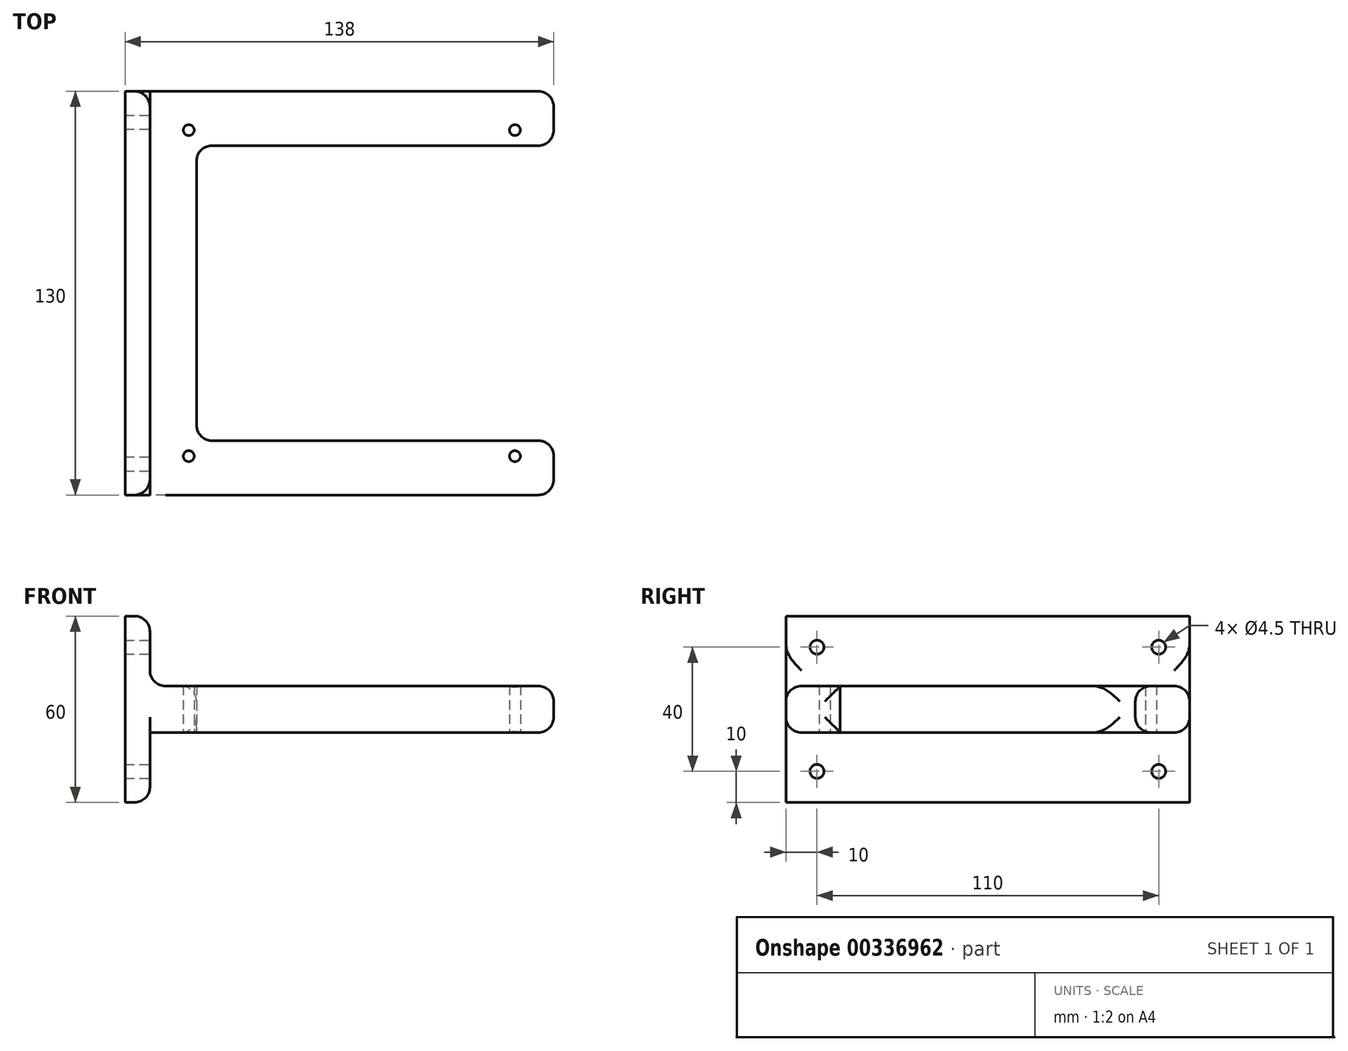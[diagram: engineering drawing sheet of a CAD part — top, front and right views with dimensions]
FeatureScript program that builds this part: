
annotation { "Feature Type Name" : "Feature", "Feature Type Description" : "" }
export const myFeature = defineFeature(function(context is Context, id is Id, definition is map)
    precondition{}
    {
        {
            var Q0;
            Q0=qCreatedBy(makeId("Top.planeOp"),FACE);
            var sketch = newSketch(context, id + "F0", { "sketchPlane" : qUnion([Q0])});
            skLineSegment(sketch, "E0.bottom", {"start": v(0, 0) * mm, "end": v(130, 0) * mm});
            skLineSegment(sketch, "E0.top", {"start": v(0, 130) * mm, "end": v(130, 130) * mm});
            skLineSegment(sketch, "E0.left", {"start": v(0, 0) * mm, "end": v(0, 130) * mm});
            skLineSegment(sketch, "E0.right", {"start": v(130, 0) * mm, "end": v(130, 130) * mm});
            skCircle(sketch, "E1", {"center": v(12.5, 12.5) * mm, "radius": 1.75 * mm});
            skCircle(sketch, "E2.0.1.0", {"center": v(12.5, 117.5) * mm, "radius": 1.75 * mm});
            skCircle(sketch, "E2.1.0.0", {"center": v(117.5, 12.5) * mm, "radius": 1.75 * mm});
            skCircle(sketch, "E2.1.1.0", {"center": v(117.5, 117.5) * mm, "radius": 1.75 * mm});
            skLineSegment(sketch, "E2.direction1", {"start": v(12.5, 12.5) * mm, "end": v(117.5, 12.5) * mm, "construction": true});
            skLineSegment(sketch, "E2.direction2", {"start": v(12.5, 12.5) * mm, "end": v(12.5, 117.5) * mm, "construction": true});
            skLineSegment(sketch, "E3.bottom", {"start": v(130, 112.5) * mm, "end": v(15, 112.5) * mm});
            skLineSegment(sketch, "E3.top", {"start": v(130, 17.5) * mm, "end": v(15, 17.5) * mm});
            skLineSegment(sketch, "E3.left", {"start": v(130, 112.5) * mm, "end": v(130, 17.5) * mm});
            skLineSegment(sketch, "E3.right", {"start": v(15, 112.5) * mm, "end": v(15, 17.5) * mm});
            skSolve(sketch);
        }
        {
            var Q0;
            {var subQ4=sQuery(id+"F0.wireOp",EDGE,"E0.bottom");Q0=makeQuery(id+"F0.imprint","IMPRINT",FACE,{"disambiguationData":[TD([[makeQuery(id+"F0.imprint","IMPRINT",EDGE,{"derivedFrom":subQ4}),1.0]])]});}
            extrude(context, id + "F1", {"entities" : qUnion([Q0]), "depth" : 15 * mm});
        }
        {
            var Q0;
            Q0=makeQuery(id+"F1.opExtrude","SWEPT_FACE",FACE,{"disambiguationData":[OSD([sQuery(id+"F0.wireOp",EDGE,"E0.left")])]});
            var sketch = newSketch(context, id + "F2", { "sketchPlane" : qUnion([Q0])});
            skPoint(sketch, "E4.oppositeSnap0", {"position": v(0, 7.5) * mm});
            skLineSegment(sketch, "E4.top", {"start": v(-130, 37.5) * mm, "end": v(0, 37.5) * mm});
            skLineSegment(sketch, "E4.left", {"start": v(-130, 7.5) * mm, "end": v(-130, 37.5) * mm});
            skLineSegment(sketch, "E4.right", {"start": v(0, 7.5) * mm, "end": v(0, 37.5) * mm});
            skLineSegment(sketch, "E5.top", {"start": v(0, -22.5) * mm, "end": v(-130, -22.5) * mm});
            skLineSegment(sketch, "E5.left", {"start": v(0, 7.5) * mm, "end": v(0, -22.5) * mm});
            skLineSegment(sketch, "E5.right", {"start": v(-130, 7.5) * mm, "end": v(-130, -22.5) * mm});
            skCircle(sketch, "E6", {"center": v(-120, -12.5) * mm, "radius": 2.25 * mm});
            skCircle(sketch, "E7.0.1.0", {"center": v(-120, 27.5) * mm, "radius": 2.25 * mm});
            skCircle(sketch, "E7.1.0.0", {"center": v(-10, -12.5) * mm, "radius": 2.25 * mm});
            skCircle(sketch, "E7.1.1.0", {"center": v(-10, 27.5) * mm, "radius": 2.25 * mm});
            skLineSegment(sketch, "E7.direction1", {"start": v(-120, -12.5) * mm, "end": v(-10, -12.5) * mm, "construction": true});
            skLineSegment(sketch, "E7.direction2", {"start": v(-120, -12.5) * mm, "end": v(-120, 27.5) * mm, "construction": true});
            skSolve(sketch);
        }
        {
            var Q0;
            {var subQ0=sQuery(id+"F2.wireOp",EDGE,"E5.top");Q0=makeQuery(id+"F2.imprint","IMPRINT",FACE,{"disambiguationData":[TD([[makeQuery(id+"F2.imprint","IMPRINT",EDGE,{"derivedFrom":subQ0}),-1.0]])]});}
            var Q1;
            {var subQ1=sQuery(id+"F0.wireOp",EDGE,"E0.left");var subQ2=makeQuery(id+"F1.opExtrude","CAP_EDGE",EDGE,{"disambiguationData":[OSD([subQ1])],"isStart":true});Q1=makeQuery(id+"F2.imprint","IMPRINT",FACE,{"disambiguationData":[TD([[makeQuery(id+"F2.imprint","IMPRINT",EDGE,{"derivedFrom":subQ2}),-1.0]])]});}
            var Q2;
            {var subQ0=sQuery(id+"F2.wireOp",EDGE,"E4.top");Q2=makeQuery(id+"F2.imprint","IMPRINT",FACE,{"disambiguationData":[TD([[makeQuery(id+"F2.imprint","IMPRINT",EDGE,{"derivedFrom":subQ0}),-1.0]])]});}
            extrude(context, id + "F3", {"entities" : qUnion([Q0, Q1, Q2]), "operationType" : NewBodyOperationType.ADD, "depth" : 8 * mm});
        }
        {
            var Q0;
            Q0=makeQuery(id+"F1.opExtrude","CAP_EDGE",EDGE,{"disambiguationData":[OSD([sQuery(id+"F0.wireOp",EDGE,"E0.left")])],"isStart":false});
            var Q1;
            Q1=makeQuery(id+"F1.opExtrude","CAP_EDGE",EDGE,{"disambiguationData":[OSD([sQuery(id+"F0.wireOp",EDGE,"E0.left")])],"isStart":true});
            var Q2;
            Q2=makeQuery(id+"F1.opExtrude","SWEPT_EDGE",EDGE,{"disambiguationData":[OSD([sQuery(id+"F0.wireOp",EDGE,"E3.bottom"),sQuery(id+"F0.wireOp",EDGE,"E3.right")])]});
            var Q3;
            Q3=makeQuery(id+"F1.opExtrude","SWEPT_EDGE",EDGE,{"disambiguationData":[OSD([sQuery(id+"F0.wireOp",EDGE,"E3.top"),sQuery(id+"F0.wireOp",EDGE,"E3.right")])]});
            var Q4;
            Q4=makeQuery(id+"F1.opExtrude","SWEPT_EDGE",EDGE,{"disambiguationData":[OSD([sQuery(id+"F0.wireOp",EDGE,"E0.right"),sQuery(id+"F0.wireOp",EDGE,"E3.top"),sQuery(id+"F0.wireOp",EDGE,"E3.left")])]});
            var Q5;
            Q5=makeQuery(id+"F1.opExtrude","SWEPT_EDGE",EDGE,{"disambiguationData":[OSD([sQuery(id+"F0.wireOp",EDGE,"E0.bottom"),sQuery(id+"F0.wireOp",EDGE,"E0.right")])]});
            var Q6;
            Q6=makeQuery(id+"F1.opExtrude","SWEPT_EDGE",EDGE,{"disambiguationData":[OSD([sQuery(id+"F0.wireOp",EDGE,"E0.top"),sQuery(id+"F0.wireOp",EDGE,"E0.right")])]});
            var Q7;
            Q7=makeQuery(id+"F1.opExtrude","SWEPT_EDGE",EDGE,{"disambiguationData":[OSD([sQuery(id+"F0.wireOp",EDGE,"E0.right"),sQuery(id+"F0.wireOp",EDGE,"E3.bottom"),sQuery(id+"F0.wireOp",EDGE,"E3.left")])]});
            var Q8;
            Q8=makeQuery(id+"F1.opExtrude","CAP_EDGE",EDGE,{"disambiguationData":[OSD([sQuery(id+"F0.wireOp",EDGE,"E3.bottom")])],"isStart":false});
            var Q9;
            Q9=makeQuery(id+"F1.opExtrude","CAP_EDGE",EDGE,{"disambiguationData":[OSD([sQuery(id+"F0.wireOp",EDGE,"E0.bottom")])],"isStart":false});
            var Q10;
            Q10=makeQuery(id+"F1.opExtrude","CAP_EDGE",EDGE,{"disambiguationData":[OSD([sQuery(id+"F0.wireOp",EDGE,"E0.top")])],"isStart":false});
            var Q11;
            Q11=makeQuery(id+"F3.opExtrude","CAP_EDGE",EDGE,{"disambiguationData":[OSD([sQuery(id+"F2.wireOp",EDGE,"E4.top")])],"isStart":true});
            var Q12;
            Q12=makeQuery(id+"F1.opExtrude","CAP_EDGE",EDGE,{"disambiguationData":[OSD([sQuery(id+"F0.wireOp",EDGE,"E0.bottom")])],"isStart":true});
            var Q13;
            Q13=makeQuery(id+"F3.opExtrude","CAP_EDGE",EDGE,{"disambiguationData":[OSD([sQuery(id+"F2.wireOp",EDGE,"E5.top")])],"isStart":true});
            var Q14;
            Q14=makeQuery(id+"F1.opExtrude","CAP_EDGE",EDGE,{"disambiguationData":[OSD([sQuery(id+"F0.wireOp",EDGE,"E0.top")])],"isStart":true});
            var Q15;
            {var subQ0=sQuery(id+"F0.wireOp",EDGE,"E0.right");Q15=makeQuery(id+"F1.opExtrude","CAP_EDGE",EDGE,{"disambiguationData":[OSD([subQ0]),TDD([makeQuery(id+"F0.imprint","IMPRINT",EDGE,{"disambiguationData":[TD([[makeQuery(id+"F0.imprint","INTERSECT",VERTEX,{"derivedFrom":[sQuery(id+"F0.wireOp",EDGE,"E0.bottom"),subQ0]}),-1.0]])],"derivedFrom":subQ0})])],"isStart":false});}
            var Q16;
            {var subQ0=sQuery(id+"F0.wireOp",EDGE,"E0.right");Q16=makeQuery(id+"F1.opExtrude","CAP_EDGE",EDGE,{"disambiguationData":[OSD([subQ0]),TDD([makeQuery(id+"F0.imprint","IMPRINT",EDGE,{"disambiguationData":[TD([[makeQuery(id+"F0.imprint","INTERSECT",VERTEX,{"derivedFrom":[sQuery(id+"F0.wireOp",EDGE,"E0.top"),subQ0]}),1.0]])],"derivedFrom":subQ0})])],"isStart":false});}
            var Q17;
            {var subQ0=sQuery(id+"F0.wireOp",EDGE,"E0.right");Q17=makeQuery(id+"F1.opExtrude","CAP_EDGE",EDGE,{"disambiguationData":[OSD([subQ0]),TDD([makeQuery(id+"F0.imprint","IMPRINT",EDGE,{"disambiguationData":[TD([[makeQuery(id+"F0.imprint","INTERSECT",VERTEX,{"derivedFrom":[sQuery(id+"F0.wireOp",EDGE,"E0.bottom"),subQ0]}),-1.0]])],"derivedFrom":subQ0})])],"isStart":true});}
            var Q18;
            {var subQ0=sQuery(id+"F0.wireOp",EDGE,"E0.right");Q18=makeQuery(id+"F1.opExtrude","CAP_EDGE",EDGE,{"disambiguationData":[OSD([subQ0]),TDD([makeQuery(id+"F0.imprint","IMPRINT",EDGE,{"disambiguationData":[TD([[makeQuery(id+"F0.imprint","INTERSECT",VERTEX,{"derivedFrom":[sQuery(id+"F0.wireOp",EDGE,"E0.top"),subQ0]}),1.0]])],"derivedFrom":subQ0})])],"isStart":true});}
            var Q19;
            Q19=makeQuery(id+"F1.opExtrude","CAP_EDGE",EDGE,{"disambiguationData":[OSD([sQuery(id+"F0.wireOp",EDGE,"E3.bottom")])],"isStart":true});
            fillet(context, id + "F4", {"entities" : qUnion([Q0, Q1, Q2, Q3, Q4, Q5, Q6, Q7, Q8, Q9, Q10, Q11, Q12, Q13, Q14, Q15, Q16, Q17, Q18, Q19]), "radius" : 5 * mm, "tangentPropagation" : true, "allowEdgeOverflow" : false});
        }
    });
